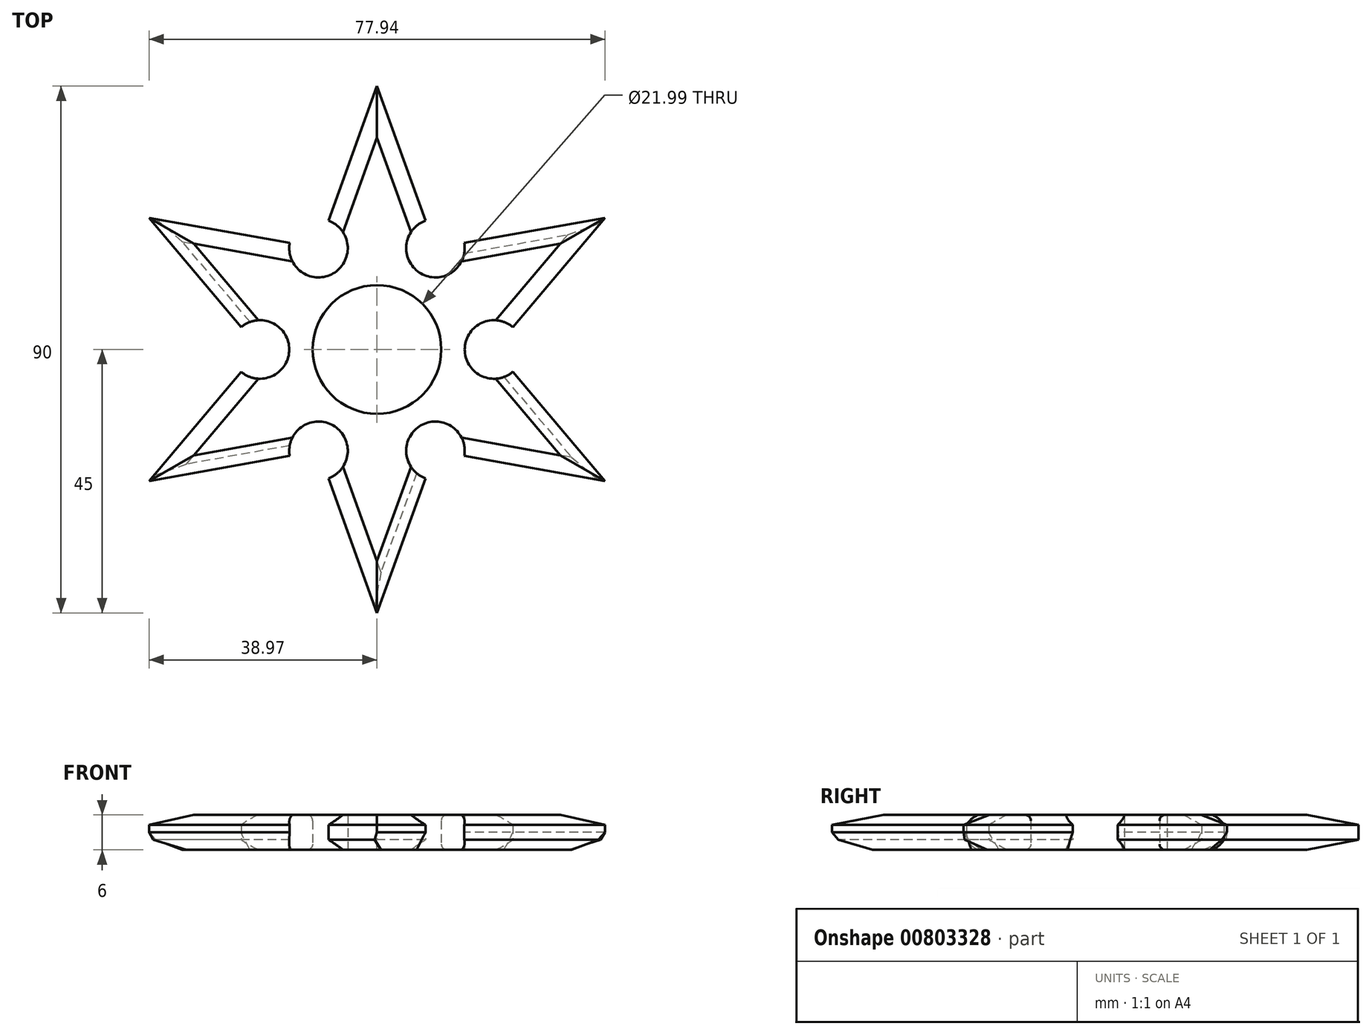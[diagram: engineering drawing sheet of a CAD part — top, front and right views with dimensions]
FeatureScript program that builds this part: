
annotation { "Feature Type Name" : "Feature", "Feature Type Description" : "" }
export const myFeature = defineFeature(function(context is Context, id is Id, definition is map)
    precondition{}
    {
        {
            var Q0;
            Q0=qCreatedBy(makeId("Top.planeOp"),FACE);
            var sketch = newSketch(context, id + "F0", { "sketchPlane" : qUnion([Q0])});
            skCircle(sketch, "E0", {"center": v(0, 0) * mm, "radius": 11 * mm});
            skLineSegment(sketch, "E1", {"start": v(0, 45) * mm, "end": v(-8.3, 22.02) * mm});
            skLineSegment(sketch, "E2.MirrorCS", {"start": v(0, 45) * mm, "end": v(8.3, 22.02) * mm});
            skLineSegment(sketch, "E3.1.0", {"start": v(-38.97, 22.5) * mm, "end": v(-14.92, 18.2) * mm});
            skLineSegment(sketch, "E3.1.1", {"start": v(-38.97, 22.5) * mm, "end": v(-23.22, 3.82) * mm});
            skLineSegment(sketch, "E3.2.0", {"start": v(-38.97, -22.5) * mm, "end": v(-23.22, -3.82) * mm});
            skLineSegment(sketch, "E3.2.1", {"start": v(-38.97, -22.5) * mm, "end": v(-14.92, -18.2) * mm});
            skLineSegment(sketch, "E3.3.0", {"start": v(0, -45) * mm, "end": v(-8.3, -22.02) * mm});
            skLineSegment(sketch, "E3.3.1", {"start": v(0, -45) * mm, "end": v(8.3, -22.02) * mm});
            skLineSegment(sketch, "E3.4.0", {"start": v(38.97, -22.5) * mm, "end": v(14.92, -18.2) * mm});
            skLineSegment(sketch, "E3.4.1", {"start": v(38.97, -22.5) * mm, "end": v(23.22, -3.82) * mm});
            skLineSegment(sketch, "E3.5.0", {"start": v(38.97, 22.5) * mm, "end": v(23.22, 3.82) * mm});
            skLineSegment(sketch, "E3.5.1", {"start": v(38.97, 22.5) * mm, "end": v(14.92, 18.2) * mm});
            skArc(sketch, "E4", {"start": v(-14.92, 18.2) * mm, "mid": v(-7.5, 12.99) * mm, "end": v(-8.3, 22.02) * mm});
            skArc(sketch, "E5.1.0", {"start": v(-23.22, -3.82) * mm, "mid": v(-15, 0) * mm, "end": v(-23.22, 3.82) * mm});
            skArc(sketch, "E5.2.0", {"start": v(-8.3, -22.02) * mm, "mid": v(-7.5, -12.99) * mm, "end": v(-14.92, -18.2) * mm});
            skArc(sketch, "E5.3.0", {"start": v(14.92, -18.2) * mm, "mid": v(7.5, -12.99) * mm, "end": v(8.3, -22.02) * mm});
            skArc(sketch, "E5.4.0", {"start": v(23.22, 3.82) * mm, "mid": v(15, 0) * mm, "end": v(23.22, -3.82) * mm});
            skArc(sketch, "E5.5.0", {"start": v(8.3, 22.02) * mm, "mid": v(7.5, 12.99) * mm, "end": v(14.92, 18.2) * mm});
            skLineSegment(sketch, "E6", {"start": v(-10, -17.32) * mm, "end": v(10, 17.32) * mm});
            skLineSegment(sketch, "E7", {"start": v(-10, 17.32) * mm, "end": v(10, -17.32) * mm});
            skLineSegment(sketch, "E8", {"start": v(-20, 0) * mm, "end": v(20, 0) * mm});
            skLineSegment(sketch, "E9", {"start": v(-23.22, 3.82) * mm, "end": v(-20, 0) * mm});
            skLineSegment(sketch, "E10", {"start": v(-20, 0) * mm, "end": v(-23.22, -3.82) * mm});
            skSolve(sketch);
        }
        {
            var Q0;
            Q0=makeQuery(id+"F0.imprint","IMPRINT",FACE,{"disambiguationData":[TD([[makeQuery(id+"F0.imprint","IMPRINT",EDGE,{"derivedFrom":sQuery(id+"F0.wireOp",EDGE,"E0")}),-1.0]])]});
            extrude(context, id + "F1", {"entities" : qUnion([Q0]), "depth" : 6 * mm, "offsetDistance" : 25 * mm});
        }
        {
            var Q0;
            Q0=makeQuery(id+"F1.opExtrude","CAP_EDGE",EDGE,{"disambiguationData":[OSD([sQuery(id+"F0.wireOp",EDGE,"E1")])],"isStart":false});
            var Q1;
            Q1=makeQuery(id+"F1.opExtrude","CAP_EDGE",EDGE,{"disambiguationData":[OSD([sQuery(id+"F0.wireOp",EDGE,"E2.MirrorCS")])],"isStart":false});
            var Q2;
            Q2=makeQuery(id+"F1.opExtrude","CAP_EDGE",EDGE,{"disambiguationData":[OSD([sQuery(id+"F0.wireOp",EDGE,"E3.5.1")])],"isStart":false});
            var Q3;
            Q3=makeQuery(id+"F1.opExtrude","CAP_EDGE",EDGE,{"disambiguationData":[OSD([sQuery(id+"F0.wireOp",EDGE,"E3.5.0")])],"isStart":false});
            var Q4;
            Q4=makeQuery(id+"F1.opExtrude","CAP_EDGE",EDGE,{"disambiguationData":[OSD([sQuery(id+"F0.wireOp",EDGE,"E3.4.1")])],"isStart":false});
            var Q5;
            Q5=makeQuery(id+"F1.opExtrude","CAP_EDGE",EDGE,{"disambiguationData":[OSD([sQuery(id+"F0.wireOp",EDGE,"E3.4.0")])],"isStart":false});
            var Q6;
            Q6=makeQuery(id+"F1.opExtrude","CAP_EDGE",EDGE,{"disambiguationData":[OSD([sQuery(id+"F0.wireOp",EDGE,"E3.3.1")])],"isStart":false});
            var Q7;
            Q7=makeQuery(id+"F1.opExtrude","CAP_EDGE",EDGE,{"disambiguationData":[OSD([sQuery(id+"F0.wireOp",EDGE,"E3.3.0")])],"isStart":false});
            var Q8;
            Q8=makeQuery(id+"F1.opExtrude","CAP_EDGE",EDGE,{"disambiguationData":[OSD([sQuery(id+"F0.wireOp",EDGE,"E3.2.1")])],"isStart":false});
            var Q9;
            Q9=makeQuery(id+"F1.opExtrude","CAP_EDGE",EDGE,{"disambiguationData":[OSD([sQuery(id+"F0.wireOp",EDGE,"E3.2.0")])],"isStart":false});
            var Q10;
            Q10=makeQuery(id+"F1.opExtrude","CAP_EDGE",EDGE,{"disambiguationData":[OSD([sQuery(id+"F0.wireOp",EDGE,"E3.1.1")])],"isStart":false});
            var Q11;
            Q11=makeQuery(id+"F1.opExtrude","CAP_EDGE",EDGE,{"disambiguationData":[OSD([sQuery(id+"F0.wireOp",EDGE,"E3.1.0")])],"isStart":false});
            var Q12;
            Q12=makeQuery(id+"F1.opExtrude","CAP_EDGE",EDGE,{"disambiguationData":[OSD([sQuery(id+"F0.wireOp",EDGE,"E3.3.1")])],"isStart":true});
            var Q13;
            Q13=makeQuery(id+"F1.opExtrude","CAP_EDGE",EDGE,{"disambiguationData":[OSD([sQuery(id+"F0.wireOp",EDGE,"E3.3.0")])],"isStart":true});
            var Q14;
            Q14=makeQuery(id+"F1.opExtrude","CAP_EDGE",EDGE,{"disambiguationData":[OSD([sQuery(id+"F0.wireOp",EDGE,"E3.2.1")])],"isStart":true});
            var Q15;
            Q15=makeQuery(id+"F1.opExtrude","CAP_EDGE",EDGE,{"disambiguationData":[OSD([sQuery(id+"F0.wireOp",EDGE,"E3.2.0")])],"isStart":true});
            var Q16;
            Q16=makeQuery(id+"F1.opExtrude","CAP_EDGE",EDGE,{"disambiguationData":[OSD([sQuery(id+"F0.wireOp",EDGE,"E3.1.1")])],"isStart":true});
            var Q17;
            Q17=makeQuery(id+"F1.opExtrude","CAP_EDGE",EDGE,{"disambiguationData":[OSD([sQuery(id+"F0.wireOp",EDGE,"E3.1.0")])],"isStart":true});
            var Q18;
            Q18=makeQuery(id+"F1.opExtrude","CAP_EDGE",EDGE,{"disambiguationData":[OSD([sQuery(id+"F0.wireOp",EDGE,"E1")])],"isStart":true});
            var Q19;
            Q19=makeQuery(id+"F1.opExtrude","CAP_EDGE",EDGE,{"disambiguationData":[OSD([sQuery(id+"F0.wireOp",EDGE,"E2.MirrorCS")])],"isStart":true});
            var Q20;
            Q20=makeQuery(id+"F1.opExtrude","CAP_EDGE",EDGE,{"disambiguationData":[OSD([sQuery(id+"F0.wireOp",EDGE,"E3.5.1")])],"isStart":true});
            var Q21;
            Q21=makeQuery(id+"F1.opExtrude","CAP_EDGE",EDGE,{"disambiguationData":[OSD([sQuery(id+"F0.wireOp",EDGE,"E3.5.0")])],"isStart":true});
            var Q22;
            Q22=makeQuery(id+"F1.opExtrude","CAP_EDGE",EDGE,{"disambiguationData":[OSD([sQuery(id+"F0.wireOp",EDGE,"E3.4.1")])],"isStart":true});
            var Q23;
            Q23=makeQuery(id+"F1.opExtrude","CAP_EDGE",EDGE,{"disambiguationData":[OSD([sQuery(id+"F0.wireOp",EDGE,"E3.4.0")])],"isStart":true});
            chamfer(context, id + "F2", {"entities" : qUnion([Q0, Q1, Q2, Q3, Q4, Q5, Q6, Q7, Q8, Q9, Q10, Q11, Q12, Q13, Q14, Q15, Q16, Q17, Q18, Q19, Q20, Q21, Q22, Q23]), "chamferType" : ChamferType.OFFSET_ANGLE, "width" : 3 * mm, "oppositeDirection" : false, "angle" : 30 * degree, "tangentPropagation" : true});
        }
        {
            var Q0;
            Q0=makeQuery(id+"F1.opExtrude","CAP_EDGE",EDGE,{"disambiguationData":[OSD([sQuery(id+"F0.wireOp",EDGE,"E0")])],"isStart":true});
            var Q1;
            Q1=makeQuery(id+"F1.opExtrude","CAP_EDGE",EDGE,{"disambiguationData":[OSD([sQuery(id+"F0.wireOp",EDGE,"E0")])],"isStart":false});
            fillet(context, id + "F3", {"entities" : qUnion([Q0, Q1]), "radius" : 1 * mm, "tangentPropagation" : true, "allowEdgeOverflow" : false});
        }
    });
